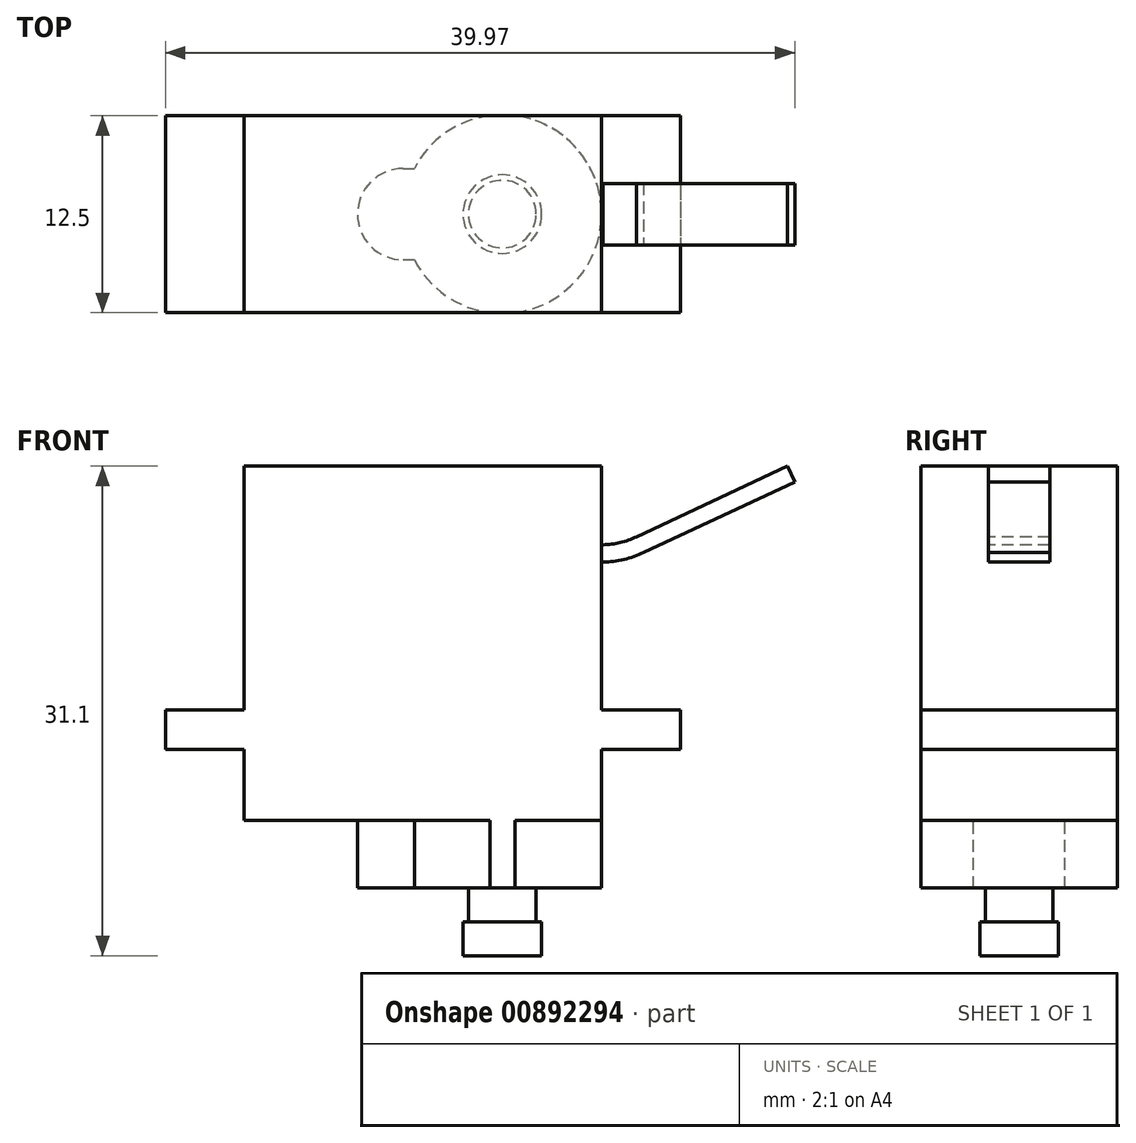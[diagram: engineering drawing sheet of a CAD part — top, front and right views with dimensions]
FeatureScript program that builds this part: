
annotation { "Feature Type Name" : "Feature", "Feature Type Description" : "" }
export const myFeature = defineFeature(function(context is Context, id is Id, definition is map)
    precondition{}
    {
        {
            var Q0;
            Q0=qCreatedBy(makeId("Top.planeOp"),FACE);
            var sketch = newSketch(context, id + "F0", { "sketchPlane" : qUnion([Q0])});
            skLineSegment(sketch, "E0.bottom", {"start": v(-4.5, 12.22) * mm, "end": v(18.2, 12.22) * mm});
            skLineSegment(sketch, "E0.top", {"start": v(-4.5, -0.28) * mm, "end": v(18.2, -0.28) * mm});
            skLineSegment(sketch, "E0.left", {"start": v(-4.5, 12.22) * mm, "end": v(-4.5, -0.28) * mm});
            skLineSegment(sketch, "E0.right", {"start": v(18.2, 12.22) * mm, "end": v(18.2, -0.28) * mm});
            skSolve(sketch);
        }
        {
            var Q0;
            Q0 = qSketchRegion(id + "F0", true);
            extrude(context, id + "F1", {"entities" : qUnion([Q0]), "depth" : 22.5 * mm, "offsetDistance" : 25 * mm});
        }
        {
            var Q0;
            Q0=makeQuery(id+"F1.opExtrude","SWEPT_FACE",FACE,{"disambiguationData":[OSD([sQuery(id+"F0.wireOp",EDGE,"E0.left")])]});
            var sketch = newSketch(context, id + "F2", { "sketchPlane" : qUnion([Q0])});
            skLineSegment(sketch, "E1.bottom", {"start": v(0.28, 4.5) * mm, "end": v(-12.22, 4.5) * mm});
            skLineSegment(sketch, "E1.top", {"start": v(0.28, 7) * mm, "end": v(-12.22, 7) * mm});
            skLineSegment(sketch, "E1.left", {"start": v(0.28, 4.5) * mm, "end": v(0.28, 7) * mm});
            skLineSegment(sketch, "E1.right", {"start": v(-12.22, 4.5) * mm, "end": v(-12.22, 7) * mm});
            skSolve(sketch);
        }
        {
            var Q0;
            Q0 = qSketchRegion(id + "F2", true);
            extrude(context, id + "F3", {"entities" : qUnion([Q0]), "operationType" : NewBodyOperationType.ADD, "depth" : 5 * mm, "offsetDistance" : 25 * mm});
        }
        {
            var Q0;
            Q0=makeQuery(id+"F1.opExtrude","SWEPT_FACE",FACE,{"disambiguationData":[OSD([sQuery(id+"F0.wireOp",EDGE,"E0.right")])]});
            var sketch = newSketch(context, id + "F4", { "sketchPlane" : qUnion([Q0])});
            skLineSegment(sketch, "E2.bottom", {"start": v(12.22, 4.5) * mm, "end": v(-0.28, 4.5) * mm});
            skLineSegment(sketch, "E2.top", {"start": v(12.22, 7) * mm, "end": v(-0.28, 7) * mm});
            skLineSegment(sketch, "E2.left", {"start": v(12.22, 4.5) * mm, "end": v(12.22, 7) * mm});
            skLineSegment(sketch, "E2.right", {"start": v(-0.28, 4.5) * mm, "end": v(-0.28, 7) * mm});
            skSolve(sketch);
        }
        {
            var Q0;
            Q0 = qSketchRegion(id + "F4", true);
            extrude(context, id + "F5", {"entities" : qUnion([Q0]), "operationType" : NewBodyOperationType.ADD, "depth" : 5 * mm, "offsetDistance" : 25 * mm});
        }
        {
            var Q0;
            Q0=makeQuery(id+"F1.opExtrude","CAP_FACE",FACE,{"disambiguationData":[OSD([sQuery(id+"F0.wireOp",EDGE,"E0.bottom"),sQuery(id+"F0.wireOp",EDGE,"E0.top"),sQuery(id+"F0.wireOp",EDGE,"E0.left"),sQuery(id+"F0.wireOp",EDGE,"E0.right")])],"isStart":true});
            var sketch = newSketch(context, id + "F6", { "sketchPlane" : qUnion([Q0])});
            skArc(sketch, "E3", {"start": v(6.28, -8.8) * mm, "mid": v(18.2, -5.97) * mm, "end": v(6.28, -3.15) * mm});
            skLineSegment(sketch, "E4", {"start": v(11.9, 0.28) * mm, "end": v(11.9, -12.22) * mm, "construction": true});
            skArc(sketch, "E5", {"start": v(5.6, -3.07) * mm, "mid": v(2.7, -5.97) * mm, "end": v(5.6, -8.87) * mm});
            skLineSegment(sketch, "E6", {"start": v(18.2, -5.97) * mm, "end": v(-4.5, -5.97) * mm, "construction": true});
            skLineSegment(sketch, "E7", {"start": v(5.6, -3.07) * mm, "end": v(6.32, -3.07) * mm});
            skPoint(sketch, "E8", {"position": v(5.6, -3.07) * mm});
            skPoint(sketch, "E9", {"position": v(6.32, -3.07) * mm});
            skLineSegment(sketch, "E10", {"start": v(5.6, -8.87) * mm, "end": v(6.32, -8.87) * mm});
            skPoint(sketch, "E11", {"position": v(6.32, -8.87) * mm});
            skPoint(sketch, "E12", {"position": v(5.6, -8.87) * mm});
            skSolve(sketch);
        }
        {
            var Q0;
            Q0=makeQuery(id+"F6.imprint","IMPRINT",FACE,{"disambiguationData":[TD([[makeQuery(id+"F6.imprint","IMPRINT",EDGE,{"derivedFrom":sQuery(id+"F6.wireOp",EDGE,"E5")}),1.0]])]});
            extrude(context, id + "F7", {"entities" : qUnion([Q0]), "operationType" : NewBodyOperationType.ADD, "depth" : 4.3 * mm, "offsetDistance" : 25 * mm});
        }
        {
            var Q0;
            Q0=makeQuery(id+"F7.opExtrude","CAP_FACE",FACE,{"disambiguationData":[OSD([sQuery(id+"F0.wireOp",EDGE,"E0.bottom"),sQuery(id+"F0.wireOp",EDGE,"E0.top"),sQuery(id+"F6.wireOp",EDGE,"E3"),sQuery(id+"F6.wireOp",EDGE,"E5"),sQuery(id+"F6.wireOp",EDGE,"E7"),sQuery(id+"F6.wireOp",EDGE,"E10")])],"isStart":false});
            var sketch = newSketch(context, id + "F8", { "sketchPlane" : qUnion([Q0])});
            skCircle(sketch, "E13", {"center": v(11.9, -5.97) * mm, "radius": 2.15 * mm});
            skSolve(sketch);
        }
        {
            var Q0;
            Q0 = qSketchRegion(id + "F8", true);
            extrude(context, id + "F9", {"entities" : qUnion([Q0]), "operationType" : NewBodyOperationType.ADD, "depth" : 2.15 * mm, "offsetDistance" : 25 * mm});
        }
        {
            var Q0;
            Q0=makeQuery(id+"F9.opExtrude","CAP_FACE",FACE,{"disambiguationData":[OSD([sQuery(id+"F8.wireOp",EDGE,"E13")])],"isStart":false});
            var sketch = newSketch(context, id + "F10", { "sketchPlane" : qUnion([Q0])});
            skCircle(sketch, "E14", {"center": v(11.9, -5.97) * mm, "radius": 2.5 * mm});
            skSolve(sketch);
        }
        {
            var Q0;
            Q0 = qSketchRegion(id + "F10", true);
            extrude(context, id + "F11", {"entities" : qUnion([Q0]), "operationType" : NewBodyOperationType.ADD, "depth" : 2.15 * mm, "offsetDistance" : 25 * mm});
        }
        {
            var Q0;
            {var subQ1=sQuery(id+"F0.wireOp",EDGE,"E0.right");Q0=makeQuery(id+"F5.boolean.opBoolean","SPLIT",FACE,{"disambiguationData":[TD([makeQuery(id+"F5.opExtrude","SWEPT_FACE",FACE,{"disambiguationData":[OSD([sQuery(id+"F4.wireOp",EDGE,"E2.top")])]})])],"derivedFrom":makeQuery(id+"F1.opExtrude","SWEPT_FACE",FACE,{"disambiguationData":[OSD([subQ1])]})});}
            var sketch = newSketch(context, id + "F12", { "sketchPlane" : qUnion([Q0])});
            skLineSegment(sketch, "E15.bottom", {"start": v(7.92, 17.5) * mm, "end": v(4.02, 17.5) * mm});
            skLineSegment(sketch, "E15.top", {"start": v(7.92, 16.4) * mm, "end": v(4.02, 16.4) * mm});
            skLineSegment(sketch, "E15.left", {"start": v(7.92, 17.5) * mm, "end": v(7.92, 16.4) * mm});
            skLineSegment(sketch, "E15.right", {"start": v(4.02, 17.5) * mm, "end": v(4.02, 16.4) * mm});
            skLineSegment(sketch, "E16", {"start": v(5.97, 22.5) * mm, "end": v(5.97, 7) * mm, "construction": true});
            skPoint(sketch, "E17", {"position": v(5.97, 17.5) * mm});
            skSolve(sketch);
        }
        {
            var Q0;
            Q0 = qSketchRegion(id + "F12", true);
            extrude(context, id + "F13", {"entities" : qUnion([Q0]), "operationType" : NewBodyOperationType.ADD, "depth" : .1 * mm, "offsetDistance" : 25 * mm});
        }
        {
            var Q0;
            Q0=makeQuery(id+"F13.opExtrude","CAP_FACE",FACE,{"disambiguationData":[OSD([sQuery(id+"F12.wireOp",EDGE,"E15.bottom"),sQuery(id+"F12.wireOp",EDGE,"E15.top"),sQuery(id+"F12.wireOp",EDGE,"E15.left"),sQuery(id+"F12.wireOp",EDGE,"E15.right")])],"isStart":false});
            var Q1;
            Q1=makeQuery(id+"F1.opExtrude","CAP_EDGE",EDGE,{"disambiguationData":[OSD([sQuery(id+"F0.wireOp",EDGE,"E0.right")])],"isStart":false});
            revolve(context, id + "F14", {"operationType" : NewBodyOperationType.ADD, "surfaceOperationType" : NewSurfaceOperationType.NEW, "entities" : qUnion([Q0]), "axis" : qUnion([Q1]), "revolveType" : RevolveType.ONE_DIRECTION, "angle" : 25 * degree});
        }
        {
            var Q0;
            Q0=makeQuery(id+"F14.opRevolve","CAP_FACE",FACE,{"disambiguationData":[OSD([sQuery(id+"F12.wireOp",EDGE,"E15.bottom"),sQuery(id+"F12.wireOp",EDGE,"E15.top"),sQuery(id+"F12.wireOp",EDGE,"E15.left"),sQuery(id+"F12.wireOp",EDGE,"E15.right")])],"isStart":false});
            var sketch = newSketch(context, id + "F15", { "sketchPlane" : qUnion([Q0])});
            skLineSegment(sketch, "E18.0", {"start": v(7.92, 6.6) * mm, "end": v(4.02, 6.6) * mm});
            skLineSegment(sketch, "E18.1", {"start": v(7.92, 7.7) * mm, "end": v(7.92, 6.6) * mm});
            skLineSegment(sketch, "E18.2", {"start": v(7.92, 7.7) * mm, "end": v(4.02, 7.7) * mm});
            skLineSegment(sketch, "E18.3", {"start": v(4.02, 7.7) * mm, "end": v(4.02, 6.6) * mm});
            skSolve(sketch);
        }
        {
            var Q0;
            Q0 = qSketchRegion(id + "F15", true);
            extrude(context, id + "F16", {"entities" : qUnion([Q0]), "operationType" : NewBodyOperationType.ADD, "depth" : 10.6 * mm, "offsetDistance" : 25 * mm});
        }
    });
